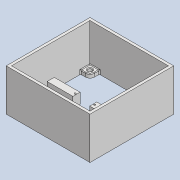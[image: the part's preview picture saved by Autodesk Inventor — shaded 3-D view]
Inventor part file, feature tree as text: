
AUTODESK INVENTOR PART (.ipt)
format: ipt  version: 2022 (Build 260153000, 153)  size: 306,688 bytes
history: native  units: in
note: dims shown in document units (in); Inventor stores cm internally (conversion verified against a paired STEP export)
features: extrude x7, sketch x6, chamfer x2, pattern_circular x1, fillet x1, plane x1, projected_geometry x1
ambient origin geometry x8: Origin, YZ Plane, XZ Plane, XY Plane, X Axis, Y Axis, Z Axis, Center Point
bodies: Solid1 (feature_tree)
feature tree (19):
  sketch  "Sketch1"  dims[d0=4.0in d1=4.0in]
  extrude  "Extrusion1"  Depth=4.0in
  extrude  "Extrusion2"  Depth=0.125in
  pattern_circular  "Circular Pattern1"  Count=4 Angle=360.0deg
  chamfer  "Chamfer4"  Distance=0.125in Angle=45.0deg
  extrude  "Extrusion3"  Depth=0.34in
  extrude  "Extrusion4"  Depth=1.717in
  extrude  "Extrusion5"  Depth=0.34in
  extrude  "Extrusion6"  Depth=0.375in
  chamfer  "Chamfer5"  Distance=0.066in
  fillet  "Fillet1"  Radius=0.08in
  extrude  "Extrusion7"  Depth=0.375in
  plane  "Work Plane1"
  sketch  "Sketch2"  dims[d2=0.125in d3=0.201in]
  projected_geometry  "Projected Loop1"
  sketch  "Sketch3"  dims[d4=0.125in]
  sketch  "Sketch4"  dims[d5=1.25in d6=0.0in]
  sketch  "Sketch5"  dims[d7=0.1875in d8=0.0in d18=1.5748in d19=360.0deg d21=0.0312in d22=0.125in d23=45.0deg]
  sketch  "Sketch6"  dims[d24=1.232in d25=0.34in d26=1.717in d27=0.34in d28=0.08in d29=0.066in d30=0.08in d31=0.066in d32=0.5in d33=0.0in d34=0.095in d35=0.095in d36=0.125in d37=0.125in d38=0.125in d39=0.0in d40=0.125in d41=0.625in d42=0.0in d44=0.75in d46=0.5in d47=0.125in d48=0.0in d49=0.0312in d50=0.125in d51=45.0deg d52=0.0625in d53=0.125in d54=0.208in d55=0.375in d56=0.0in]
